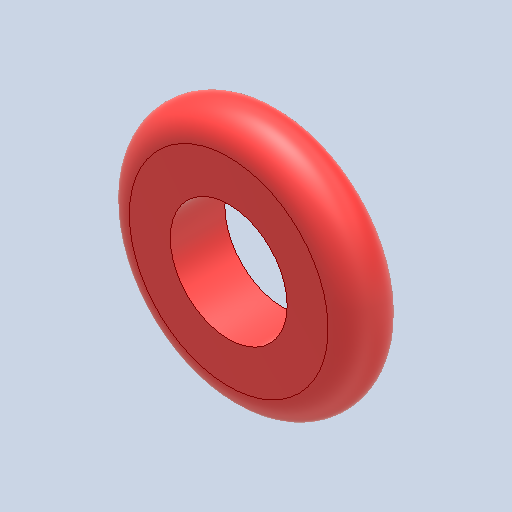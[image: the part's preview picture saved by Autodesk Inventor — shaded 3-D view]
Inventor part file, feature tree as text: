
AUTODESK INVENTOR PART (.ipt)
format: ipt  version: 2023 (Build 270158030, 158C)  size: 154,112 bytes
history: native  units: mm
features: other x1, extrude x1, fillet x1, sketch x1
ambient origin geometry x8: Origin, YZ Plane, XZ Plane, XY Plane, X Axis, Y Axis, Z Axis, Center Point
bodies: Body1 (feature_tree)
feature tree (4):
  other  "ソリッド1"
  extrude  "押し出し1"  Depth=6.5mm
  fillet  "フィレット1"  Radius=3.0mm
  sketch  "スケッチ1"
